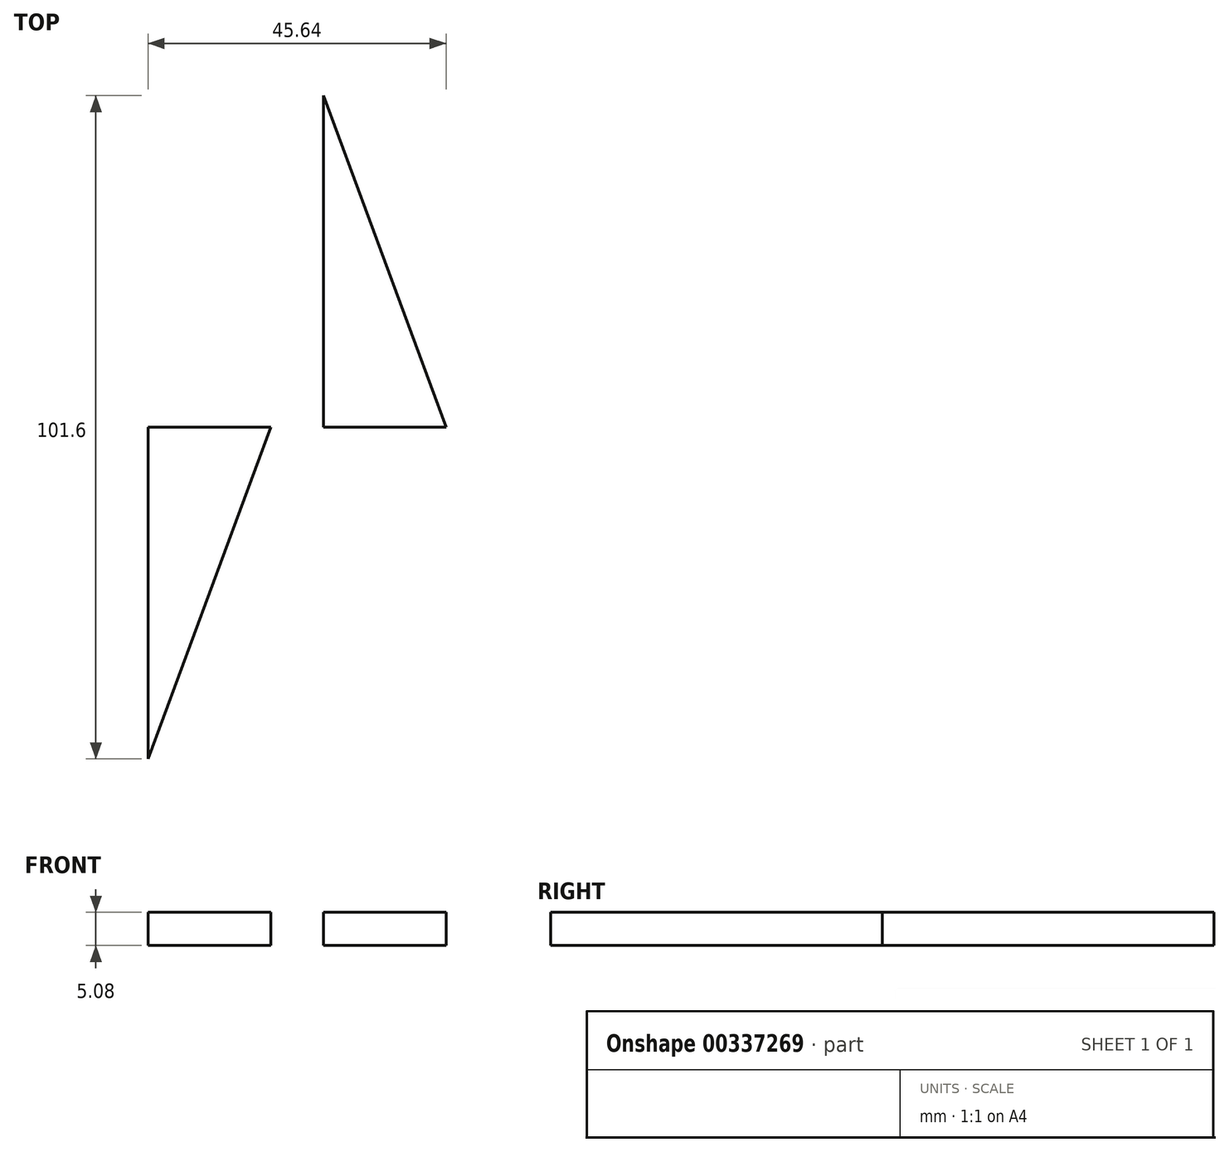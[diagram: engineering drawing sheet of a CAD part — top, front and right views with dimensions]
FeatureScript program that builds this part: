
annotation { "Feature Type Name" : "Feature", "Feature Type Description" : "" }
export const myFeature = defineFeature(function(context is Context, id is Id, definition is map)
    precondition{}
    {
        {
            var Q0;
            Q0=qCreatedBy(makeId("Top.planeOp"),FACE);
            var sketch = newSketch(context, id + "F0", { "sketchPlane" : qUnion([Q0])});
            skLineSegment(sketch, "E0", {"start": v(-48.67, 0) * mm, "end": v(-48.67, -50.8) * mm});
            skLineSegment(sketch, "E1", {"start": v(-48.67, -50.8) * mm, "end": v(-29.87, 0) * mm});
            skLineSegment(sketch, "E2", {"start": v(-48.67, 0) * mm, "end": v(-29.87, 0) * mm});
            skSolve(sketch);
        }
        {
            var Q0;
            Q0=makeQuery(id+"F0.imprint","IMPRINT",FACE,{"disambiguationData":[TD([[makeQuery(id+"F0.imprint","IMPRINT",EDGE,{"derivedFrom":sQuery(id+"F0.wireOp",EDGE,"E0")}),1.0]])]});
            extrude(context, id + "F1", {"entities" : qUnion([Q0]), "depth" : 5.08 * mm});
        }
        {
            var Q0;
            Q0=qCreatedBy(makeId("Top.planeOp"),FACE);
            var sketch = newSketch(context, id + "F2", { "sketchPlane" : qUnion([Q0])});
            skLineSegment(sketch, "E3", {"start": v(-21.83, 0) * mm, "end": v(-3.03, 0) * mm});
            skLineSegment(sketch, "E4", {"start": v(-21.83, 0) * mm, "end": v(-21.83, 50.8) * mm});
            skLineSegment(sketch, "E5", {"start": v(-21.83, 50.8) * mm, "end": v(-3.03, 0) * mm});
            skSolve(sketch);
        }
        {
            var Q0;
            Q0=makeQuery(id+"F2.imprint","IMPRINT",FACE,{"disambiguationData":[TD([[makeQuery(id+"F2.imprint","IMPRINT",EDGE,{"derivedFrom":sQuery(id+"F2.wireOp",EDGE,"E3")}),1.0]])]});
            extrude(context, id + "F3", {"entities" : qUnion([Q0]), "depth" : 5.08 * mm});
        }
    });
